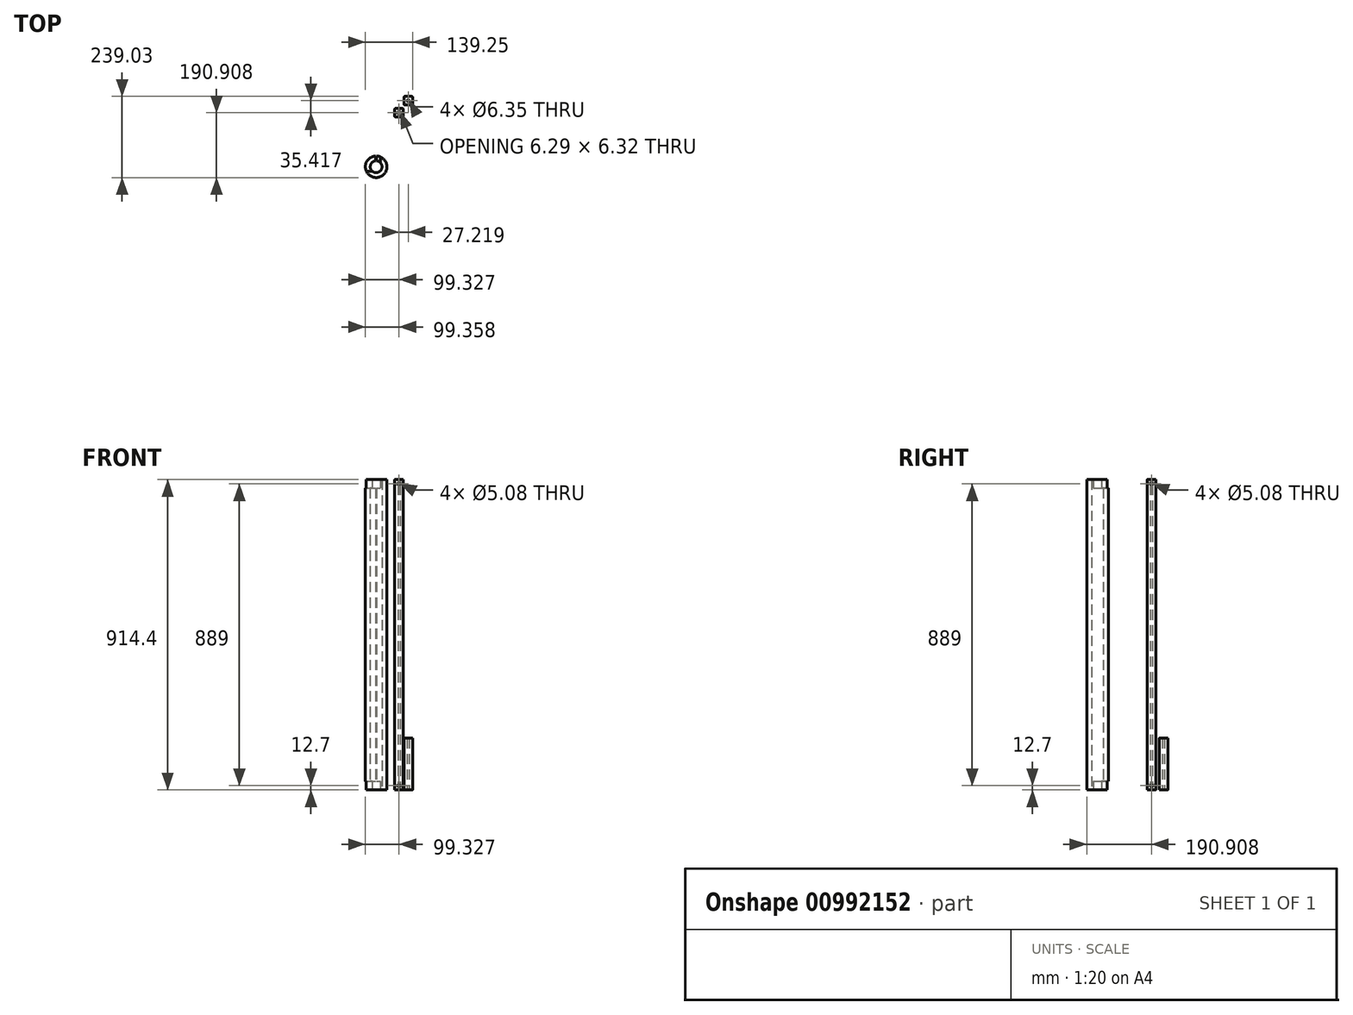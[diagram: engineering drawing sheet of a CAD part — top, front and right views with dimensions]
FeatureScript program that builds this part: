
annotation { "Feature Type Name" : "Feature", "Feature Type Description" : "" }
export const myFeature = defineFeature(function(context is Context, id is Id, definition is map)
    precondition{}
    {
        {
            var Q0;
            Q0=qCreatedBy(makeId("Top.planeOp"),FACE);
            var sketch = newSketch(context, id + "F0", { "sketchPlane" : qUnion([Q0])});
            skLineSegment(sketch, "E0.bottom", {"start": v(-88.3, 28.05) * mm, "end": v(-108.62, 28.05) * mm});
            skLineSegment(sketch, "E0.top", {"start": v(-88.3, 53.45) * mm, "end": v(-108.62, 53.45) * mm});
            skLineSegment(sketch, "E0.left", {"start": v(-85.76, 30.59) * mm, "end": v(-85.76, 50.9) * mm});
            skLineSegment(sketch, "E0.right", {"start": v(-111.16, 30.59) * mm, "end": v(-111.16, 50.9) * mm});
            skPoint(sketch, "E0.middle", {"position": v(-98.46, 40.75) * mm});
            skPoint(sketch, "E1.visualSharp", {"position": v(-111.16, 53.45) * mm});
            skArc(sketch, "E1.filletArc", {"start": v(-108.62, 53.45) * mm, "mid": v(-110.42, 52.7) * mm, "end": v(-111.16, 50.9) * mm});
            skPoint(sketch, "E2.visualSharp", {"position": v(-85.76, 53.45) * mm});
            skArc(sketch, "E2.filletArc", {"start": v(-85.76, 50.9) * mm, "mid": v(-86.5, 52.7) * mm, "end": v(-88.3, 53.45) * mm});
            skPoint(sketch, "E3.visualSharp", {"position": v(-85.76, 28.05) * mm});
            skArc(sketch, "E3.filletArc", {"start": v(-88.3, 28.05) * mm, "mid": v(-86.5, 28.8) * mm, "end": v(-85.76, 30.59) * mm});
            skPoint(sketch, "E4.visualSharp", {"position": v(-111.16, 28.05) * mm});
            skArc(sketch, "E4.filletArc", {"start": v(-111.16, 30.59) * mm, "mid": v(-110.42, 28.8) * mm, "end": v(-108.62, 28.05) * mm});
            skCircle(sketch, "E5", {"center": v(-98.46, 40.75) * mm, "radius": 3.18 * mm});
            skSolve(sketch);
        }
        {
            var Q0;
            Q0 = qSketchRegion(id + "F0", true);
            extrude(context, id + "F1", {"entities" : qUnion([Q0]), "depth" : 914.4 * mm, "offsetDistance" : 25.4 * mm});
        }
        {
            var Q0;
            Q0=qCreatedBy(makeId("Top.planeOp"),FACE);
            var sketch = newSketch(context, id + "F2", { "sketchPlane" : qUnion([Q0])});
            skLineSegment(sketch, "E6.bottom", {"start": v(-61.08, 63.47) * mm, "end": v(-81.4, 63.47) * mm});
            skLineSegment(sketch, "E6.top", {"start": v(-61.08, 88.87) * mm, "end": v(-81.4, 88.87) * mm});
            skLineSegment(sketch, "E6.left", {"start": v(-58.54, 66) * mm, "end": v(-58.54, 86.33) * mm});
            skLineSegment(sketch, "E6.right", {"start": v(-83.94, 66) * mm, "end": v(-83.94, 86.33) * mm});
            skPoint(sketch, "E6.middle", {"position": v(-71.24, 76.17) * mm});
            skPoint(sketch, "E7.visualSharp", {"position": v(-83.94, 88.87) * mm});
            skArc(sketch, "E7.filletArc", {"start": v(-81.4, 88.87) * mm, "mid": v(-83.2, 88.12) * mm, "end": v(-83.94, 86.33) * mm});
            skPoint(sketch, "E8.visualSharp", {"position": v(-58.54, 88.87) * mm});
            skArc(sketch, "E8.filletArc", {"start": v(-58.54, 86.33) * mm, "mid": v(-59.29, 88.12) * mm, "end": v(-61.08, 88.87) * mm});
            skPoint(sketch, "E9.visualSharp", {"position": v(-58.54, 63.47) * mm});
            skArc(sketch, "E9.filletArc", {"start": v(-61.08, 63.47) * mm, "mid": v(-59.29, 64.2) * mm, "end": v(-58.54, 66) * mm});
            skPoint(sketch, "E10.visualSharp", {"position": v(-83.94, 63.47) * mm});
            skArc(sketch, "E10.filletArc", {"start": v(-83.94, 66) * mm, "mid": v(-83.2, 64.2) * mm, "end": v(-81.4, 63.47) * mm});
            skCircle(sketch, "E11", {"center": v(-71.24, 76.17) * mm, "radius": 3.18 * mm});
            skSolve(sketch);
        }
        {
            var Q0;
            Q0 = qSketchRegion(id + "F2", true);
            extrude(context, id + "F3", {"entities" : qUnion([Q0]), "depth" : 152.4 * mm, "offsetDistance" : 25.4 * mm});
        }
        {
            var Q0;
            Q0=makeQuery(id+"F1.opExtrude","SWEPT_FACE",FACE,{"disambiguationData":[OSD([sQuery(id+"F0.wireOp",EDGE,"E0.bottom")])]});
            var sketch = newSketch(context, id + "F4", { "sketchPlane" : qUnion([Q0])});
            skLineSegment(sketch, "E12", {"start": v(-98.46, 914.4) * mm, "end": v(-98.46, 901.7) * mm, "construction": true});
            skLineSegment(sketch, "E13", {"start": v(-98.46, 0) * mm, "end": v(-98.46, 12.7) * mm, "construction": true});
            skCircle(sketch, "E14", {"center": v(-98.46, 12.7) * mm, "radius": 2.54 * mm});
            skCircle(sketch, "E15", {"center": v(-98.46, 901.7) * mm, "radius": 2.54 * mm});
            skSolve(sketch);
        }
        {
            var Q0;
            Q0 = qSketchRegion(id + "F4", true);
            extrude(context, id + "F5", {"entities" : qUnion([Q0]), "operationType" : NewBodyOperationType.REMOVE, "oppositeDirection" : true, "depth" : 25.4 * mm, "offsetDistance" : 25.4 * mm});
        }
        {
            var Q0;
            Q0=makeQuery(id+"F1.opExtrude","SWEPT_FACE",FACE,{"disambiguationData":[OSD([sQuery(id+"F0.wireOp",EDGE,"E0.left")])]});
            var sketch = newSketch(context, id + "F6", { "sketchPlane" : qUnion([Q0])});
            skLineSegment(sketch, "E16", {"start": v(40.75, 914.4) * mm, "end": v(40.75, 901.7) * mm, "construction": true});
            skLineSegment(sketch, "E17", {"start": v(40.75, 0) * mm, "end": v(40.75, 12.7) * mm, "construction": true});
            skCircle(sketch, "E18", {"center": v(40.75, 12.7) * mm, "radius": 2.54 * mm});
            skCircle(sketch, "E19", {"center": v(40.75, 901.7) * mm, "radius": 2.54 * mm});
            skSolve(sketch);
        }
        {
            var Q0;
            Q0 = qSketchRegion(id + "F6", true);
            extrude(context, id + "F7", {"entities" : qUnion([Q0]), "operationType" : NewBodyOperationType.REMOVE, "oppositeDirection" : true, "depth" : 25.4 * mm, "offsetDistance" : 25.4 * mm});
        }
        {
            var Q0;
            Q0=qCreatedBy(makeId("Top.planeOp"),FACE);
            var sketch = newSketch(context, id + "F8", { "sketchPlane" : qUnion([Q0])});
            skArc(sketch, "E20", {"start": v(-167.31, -86.69) * mm, "mid": v(-166.04, -150.16) * mm, "end": v(-164.77, -86.69) * mm});
            skArc(sketch, "E21", {"start": v(-167.31, -101) * mm, "mid": v(-166.04, -135.87) * mm, "end": v(-164.77, -101) * mm});
            skLineSegment(sketch, "E22.left", {"start": v(-167.31, -86.69) * mm, "end": v(-167.31, -101) * mm});
            skLineSegment(sketch, "E22.right", {"start": v(-164.77, -86.69) * mm, "end": v(-164.77, -101) * mm});
            skSolve(sketch);
        }
        {
            var Q0;
            Q0 = qSketchRegion(id + "F8", true);
            extrude(context, id + "F9", {"entities" : qUnion([Q0]), "depth" : 914.4 * mm, "offsetDistance" : 25.4 * mm});
        }
        {
            var Q0;
            Q0=makeQuery(id+"F9.opExtrude","SWEPT_EDGE",EDGE,{"disambiguationData":[OSD([sQuery(id+"F8.wireOp",EDGE,"E21"),sQuery(id+"F8.wireOp",EDGE,"E22.left")])]});
            cPlane(context, id + "F10", {"entities" : qUnion([Q0]), "cplaneType" : CPlaneType.LINE_ANGLE, "offset" : 25.4 * mm, "angle" : 90 * degree, "width" : 152.4 * mm, "height" : 152.4 * mm});
        }
        {
            var Q0;
            Q0=qCreatedBy(id+"F10.planeOp",FACE);
            var sketch = newSketch(context, id + "F11", { "sketchPlane" : qUnion([Q0])});
            skPoint(sketch, "E23.middle", {"position": v(166.04, 914.4) * mm});
            skPoint(sketch, "E24.middle", {"position": v(166.04, 0) * mm});
            skLineSegment(sketch, "E25.bottom", {"start": v(178.74, -25.4) * mm, "end": v(153.34, -25.4) * mm});
            skLineSegment(sketch, "E25.top", {"start": v(178.74, 25.4) * mm, "end": v(153.34, 25.4) * mm});
            skLineSegment(sketch, "E25.left", {"start": v(178.74, -25.4) * mm, "end": v(178.74, 25.4) * mm});
            skLineSegment(sketch, "E25.right", {"start": v(153.34, -25.4) * mm, "end": v(153.34, 25.4) * mm});
            skLineSegment(sketch, "E26.bottom", {"start": v(178.74, 25.4) * mm, "end": v(204.14, 25.4) * mm});
            skLineSegment(sketch, "E26.top", {"start": v(178.74, -25.4) * mm, "end": v(204.14, -25.4) * mm});
            skLineSegment(sketch, "E26.left", {"start": v(178.74, 25.4) * mm, "end": v(178.74, -25.4) * mm});
            skLineSegment(sketch, "E26.right", {"start": v(204.14, 25.4) * mm, "end": v(204.14, -25.4) * mm});
            skLineSegment(sketch, "E27.bottom", {"start": v(178.74, 939.8) * mm, "end": v(153.34, 939.8) * mm});
            skLineSegment(sketch, "E27.top", {"start": v(178.74, 889) * mm, "end": v(153.34, 889) * mm});
            skLineSegment(sketch, "E27.left", {"start": v(178.74, 939.8) * mm, "end": v(178.74, 889) * mm});
            skLineSegment(sketch, "E27.right", {"start": v(153.34, 939.8) * mm, "end": v(153.34, 889) * mm});
            skLineSegment(sketch, "E28.bottom", {"start": v(178.74, 939.8) * mm, "end": v(204.14, 939.8) * mm});
            skLineSegment(sketch, "E28.top", {"start": v(178.74, 889) * mm, "end": v(204.14, 889) * mm});
            skLineSegment(sketch, "E28.right", {"start": v(204.14, 939.8) * mm, "end": v(204.14, 889) * mm});
            skSolve(sketch);
        }
        {
            var Q0;
            Q0 = qSketchRegion(id + "F11", true);
            extrude(context, id + "F12", {"entities" : qUnion([Q0]), "operationType" : NewBodyOperationType.REMOVE, "endBound" : BoundingType.SYMMETRIC, "depth" : 60.32 * mm, "offsetDistance" : 25.4 * mm});
        }
    });
